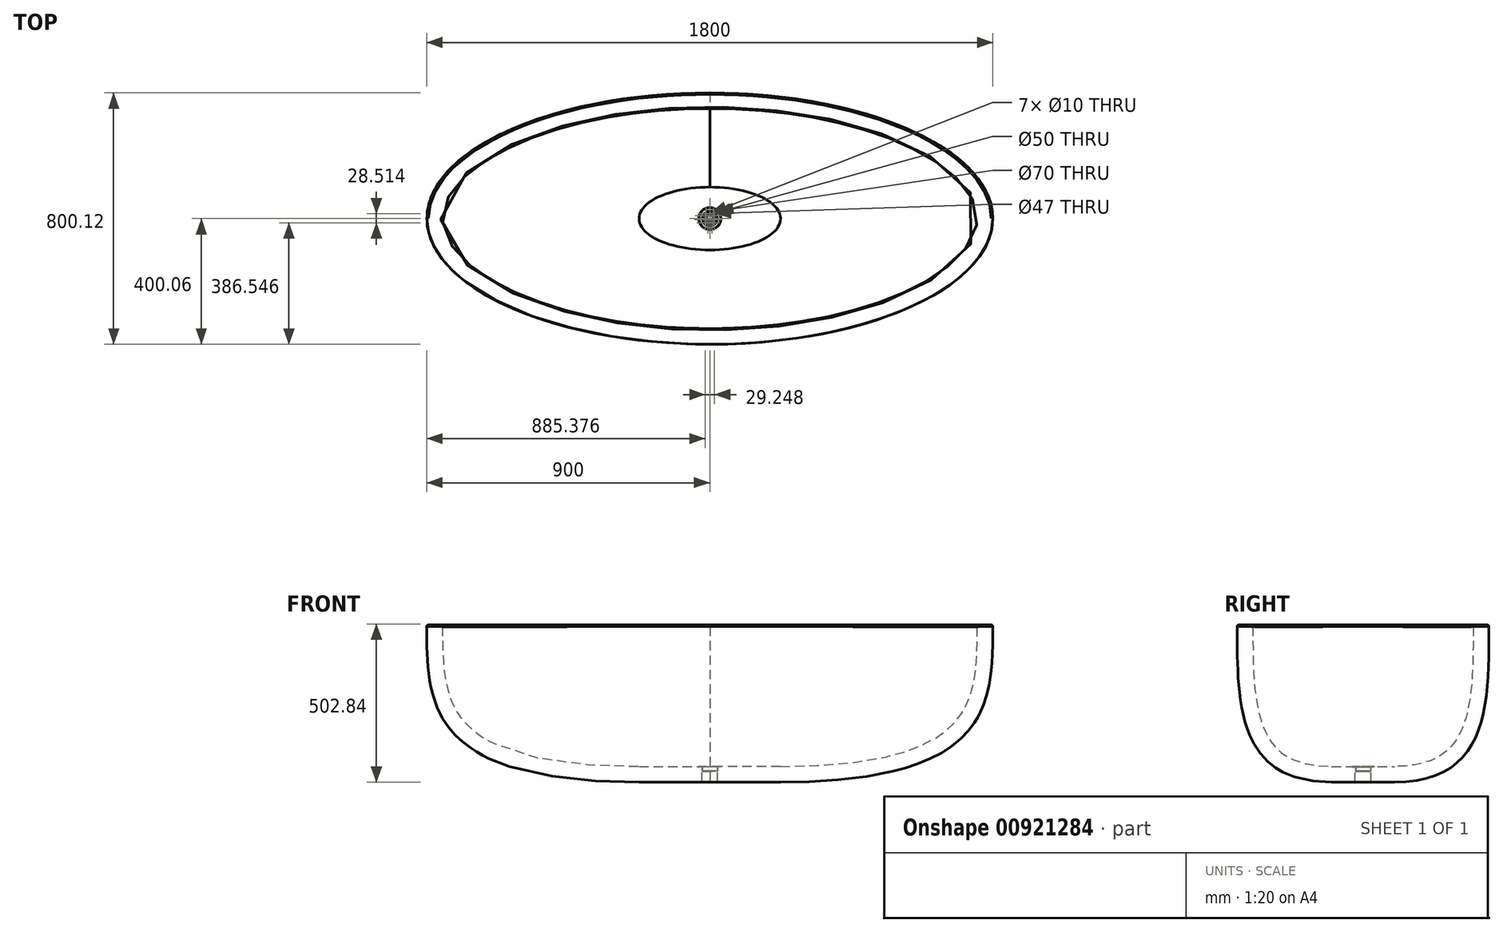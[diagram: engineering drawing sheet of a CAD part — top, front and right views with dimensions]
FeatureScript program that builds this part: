
annotation { "Feature Type Name" : "Feature", "Feature Type Description" : "" }
export const myFeature = defineFeature(function(context is Context, id is Id, definition is map)
    precondition{}
    {
        {
            var Q0;
            Q0=qCreatedBy(makeId("Top.planeOp"),FACE);
            cPlane(context, id + "F0", {"entities" : qUnion([Q0]), "cplaneType" : CPlaneType.OFFSET, "offset" : 500 * mm, "oppositeDirection" : true, "width" : 150 * mm, "height" : 150 * mm});
        }
        {
            var Q0;
            Q0=qCreatedBy(makeId("Top.planeOp"),FACE);
            var sketch = newSketch(context, id + "F1", { "sketchPlane" : qUnion([Q0])});
            skEllipse(sketch, "E0", {"center": v(0, 0) * mm, "majorRadius": 900 * mm, "minorRadius": 400 * mm, "majorAxis": v(-1, 0)});
            skSolve(sketch);
        }
        {
            var Q0;
            Q0=qCreatedBy(id+"F0.planeOp",FACE);
            var sketch = newSketch(context, id + "F2", { "sketchPlane" : qUnion([Q0])});
            skEllipse(sketch, "E1", {"center": v(0, 0) * mm, "majorRadius": 225 * mm, "minorRadius": 100 * mm, "majorAxis": v(1, 0)});
            skSolve(sketch);
        }
        {
            var Q0;
            Q0=qCreatedBy(makeId("Front.planeOp"),FACE);
            var sketch = newSketch(context, id + "F3", { "sketchPlane" : qUnion([Q0])});
            skLineSegment(sketch, "E2", {"start": v(0, 0) * mm, "end": v(-900, 0) * mm, "construction": true});
            skLineSegment(sketch, "E3", {"start": v(0, -500) * mm, "end": v(0, 0) * mm, "construction": true});
            skLineSegment(sketch, "E4", {"start": v(-225, -500) * mm, "end": v(-900, -500) * mm, "construction": true});
            skLineSegment(sketch, "E5", {"start": v(-900, 0) * mm, "end": v(-900, -500) * mm, "construction": true});
            skFitSpline(sketch, "E6", {"points": [v(-225, -500) * mm, v(-900, 0) * mm], "startDerivative": vector(-2025, 0) * mm, "endDerivative": vector(0, 750) * mm});
            skFitSpline(sketch, "E7.MirrorCS", {"points": [v(225, -500) * mm, v(900, 0) * mm], "startDerivative": vector(2025, 0) * mm, "endDerivative": vector(0, 750) * mm});
            skSolve(sketch);
        }
        {
            var Q0;
            Q0=qCreatedBy(makeId("Right.planeOp"),FACE);
            var sketch = newSketch(context, id + "F4", { "sketchPlane" : qUnion([Q0])});
            skLineSegment(sketch, "E8", {"start": v(0, 0) * mm, "end": v(-400, 0) * mm, "construction": true});
            skLineSegment(sketch, "E9", {"start": v(0, -376.84) * mm, "end": v(0, 0) * mm, "construction": true});
            skFitSpline(sketch, "E10.MirrorCS", {"points": [v(100, -500) * mm, v(400, 0) * mm], "startDerivative": vector(905.15, 0) * mm, "endDerivative": vector(-1.98, 750) * mm});
            skLineSegment(sketch, "E11", {"start": v(400, 0) * mm, "end": v(400, -665.48) * mm, "construction": true});
            skFitSpline(sketch, "E12.MirrorCS", {"points": [v(-100, -500) * mm, v(-400, 0) * mm], "startDerivative": vector(-905.15, 0) * mm, "endDerivative": vector(1.98, 750) * mm});
            skSolve(sketch);
        }
        {
            var Q0;
            Q0=makeQuery(id+"F1.imprint","IMPRINT",FACE,{"disambiguationData":[TD([[makeQuery(id+"F1.imprint","IMPRINT",EDGE,{"derivedFrom":sQuery(id+"F1.wireOp",EDGE,"E0")}),1.0]])]});
            var Q1;
            Q1=makeQuery(id+"F2.imprint","IMPRINT",FACE,{"disambiguationData":[TD([[makeQuery(id+"F2.imprint","IMPRINT",EDGE,{"derivedFrom":sQuery(id+"F2.wireOp",EDGE,"E1")}),1.0]])]});
            var Q2;
            Q2=sQuery(id+"F3.wireOp",EDGE,"E7.MirrorCS");
            var Q3;
            Q3=sQuery(id+"F4.wireOp",EDGE,"E10.MirrorCS");
            var Q4;
            Q4=sQuery(id+"F3.wireOp",EDGE,"E6");
            var Q5;
            Q5=sQuery(id+"F4.wireOp",EDGE,"E12.MirrorCS");
            loft(context, id + "F5", {"addGuides" : true, "sheetProfilesArray" : [{ "sheetProfileEntities" : qUnion([Q0]) }, { "sheetProfileEntities" : qUnion([Q1]) }], "guidesArray" : [{ "guideEntities" : qUnion([Q2]), "guideDerivativeType" : LoftGuideDerivativeType.DEFAULT, "guideDerivativeMagnitude" : 1 }, { "guideEntities" : qUnion([Q3]), "guideDerivativeType" : LoftGuideDerivativeType.DEFAULT, "guideDerivativeMagnitude" : 1 }, { "guideEntities" : qUnion([Q4]), "guideDerivativeType" : LoftGuideDerivativeType.DEFAULT, "guideDerivativeMagnitude" : 1 }, { "guideEntities" : qUnion([Q5]), "guideDerivativeType" : LoftGuideDerivativeType.DEFAULT, "guideDerivativeMagnitude" : 1 }]});
        }
        {
            var Q0;
            Q0=makeQuery(id+"F5.opLoft","CAP_FACE",FACE,{"disambiguationData":[OSD([makeQuery(id+"F1.imprint","IMPRINT",FACE,{"disambiguationData":[TD([[makeQuery(id+"F1.imprint","IMPRINT",EDGE,{"derivedFrom":sQuery(id+"F1.wireOp",EDGE,"E0")}),1.0]])]})])],"isStart":true});
            shell(context, id + "F6", {"entities" : qUnion([Q0]), "thickness" : 50 * mm});
        }
        {
            var Q0;
            Q0=makeQuery(id+"F6.opShell","OFFSET_EDGE",EDGE,{"disambiguationData":[OSD([sQuery(id+"F1.wireOp",EDGE,"E0"),sQuery(id+"F3.wireOp",EDGE,"9252d075-e4b6-4dbb-adb2-d72ff0bdb84f"),sQuery(id+"F3.wireOp",EDGE,"53aed624-99b1-4971-b216-df8eaaed4a5d0.MirrorCS"),sQuery(id+"F4.wireOp",EDGE,"d5f11650-ef26-4273-afc9-098c5ead0dd9"),sQuery(id+"F4.wireOp",EDGE,"256ece40-c806-4ca6-84fc-b8a8d223247b0.MirrorCS")])]});
            var Q1;
            Q1=makeQuery(id+"F5.opLoft","MID_CAP_EDGE",EDGE,{"disambiguationData":[OSD([sQuery(id+"F1.wireOp",EDGE,"E0"),sQuery(id+"F3.wireOp",EDGE,"53aed624-99b1-4971-b216-df8eaaed4a5d0.MirrorCS"),sQuery(id+"F4.wireOp",EDGE,"d5f11650-ef26-4273-afc9-098c5ead0dd9")])],"capPos":0.0});
            fillet(context, id + "F7", {"entities" : qUnion([Q0, Q1]), "radius" : 5 * mm, "tangentPropagation" : true, "allowEdgeOverflow" : false});
        }
        {
            var Q0;
            Q0=qCreatedBy(makeId("Top.planeOp"),FACE);
            var sketch = newSketch(context, id + "F8", { "sketchPlane" : qUnion([Q0])});
            skCircle(sketch, "E13", {"center": v(0, 0) * mm, "radius": 25 * mm});
            skSolve(sketch);
        }
        {
            var Q0;
            Q0 = qSketchRegion(id + "F8", true);
            extrude(context, id + "F9", {"entities" : qUnion([Q0]), "operationType" : NewBodyOperationType.REMOVE, "endBound" : BoundingType.THROUGH_ALL, "oppositeDirection" : true, "depth" : 25 * mm, "offsetDistance" : 25 * mm});
        }
        {
            var Q0;
            Q0=makeQuery(id+"F1.imprint","IMPRINT",FACE,{"disambiguationData":[TD([[makeQuery(id+"F1.imprint","IMPRINT",EDGE,{"derivedFrom":sQuery(id+"F1.wireOp",EDGE,"E0")}),1.0]])]});
            var sketch = newSketch(context, id + "F10", { "sketchPlane" : qUnion([Q0])});
            skCircle(sketch, "E14", {"center": v(0, 0) * mm, "radius": 35 * mm});
            skSolve(sketch);
        }
        {
            var Q0;
            Q0 = qSketchRegion(id + "F10", true);
            extrude(context, id + "F11", {"entities" : qUnion([Q0]), "operationType" : NewBodyOperationType.REMOVE, "oppositeDirection" : true, "depth" : 451.5 * mm, "offsetDistance" : 25 * mm});
        }
        {
            var Q0;
            Q0=makeQuery(id+"F11.boolean.opBoolean","INTERSECT",EDGE,{"derivedFrom":[makeQuery(id+"F6.opShell","OFFSET_FACE",FACE,{"disambiguationData":[OSD([makeQuery(id+"F2.imprint","IMPRINT",FACE,{"disambiguationData":[TD([[makeQuery(id+"F2.imprint","IMPRINT",EDGE,{"derivedFrom":sQuery(id+"F2.wireOp",EDGE,"E1")}),1.0]])]})])]}),makeQuery(id+"F11.opExtrude","SWEPT_FACE",FACE,{"disambiguationData":[OSD([sQuery(id+"F10.wireOp",EDGE,"E14")])]})]});
            var Q1;
            Q1=makeQuery(id+"F11.boolean.opBoolean","COPY",EDGE,{"derivedFrom":makeQuery(id+"F11.opExtrude","CAP_EDGE",EDGE,{"disambiguationData":[OSD([sQuery(id+"F10.wireOp",EDGE,"E14")])],"isStart":false})});
            var Q2;
            Q2=makeQuery(id+"F11.boolean.opBoolean","INTERSECT",EDGE,{"derivedFrom":[makeQuery(id+"F9.boolean.opBoolean","COPY",FACE,{"derivedFrom":makeQuery(id+"F9.opExtrude","SWEPT_FACE",FACE,{"disambiguationData":[OSD([sQuery(id+"F8.wireOp",EDGE,"E13")])]})}),makeQuery(id+"F11.opExtrude","CAP_FACE",FACE,{"disambiguationData":[OSD([sQuery(id+"F10.wireOp",EDGE,"E14")])],"isStart":false})]});
            fillet(context, id + "F12", {"entities" : qUnion([Q0, Q1, Q2]), "radius" : 0.5 * mm, "tangentPropagation" : true, "allowEdgeOverflow" : false});
        }
        {
            var Q0;
            Q0=qCreatedBy(makeId("Front.planeOp"),FACE);
            var sketch = newSketch(context, id + "F13", { "sketchPlane" : qUnion([Q0])});
            skLineSegment(sketch, "E15", {"start": v(-34.5, -450) * mm, "end": v(-34.5, -451) * mm});
            skLineSegment(sketch, "E16", {"start": v(-34.5, -451) * mm, "end": v(-25.5, -451) * mm});
            skLineSegment(sketch, "E17", {"start": v(-24.5, -452) * mm, "end": v(-24.5, -464.08) * mm});
            skLineSegment(sketch, "E18", {"start": v(-22.5, -466.08) * mm, "end": v(0, -466.08) * mm});
            skPoint(sketch, "E19.visualSharp", {"position": v(-24.5, -466.08) * mm});
            skArc(sketch, "E19.filletArc", {"start": v(-24.5, -464.08) * mm, "mid": v(-23.91, -465.5) * mm, "end": v(-22.5, -466.08) * mm});
            skPoint(sketch, "E20.visualSharp", {"position": v(-24.5, -451) * mm});
            skArc(sketch, "E20.filletArc", {"start": v(-24.5, -452) * mm, "mid": v(-24.8, -451.3) * mm, "end": v(-25.5, -451) * mm});
            skArc(sketch, "E21.0", {"start": v(-23.5, -452) * mm, "mid": v(-24.09, -450.59) * mm, "end": v(-25.5, -450) * mm});
            skLineSegment(sketch, "E21.1", {"start": v(-34.5, -450) * mm, "end": v(-25.5, -450) * mm});
            skLineSegment(sketch, "E22.0", {"start": v(-23.5, -452) * mm, "end": v(-23.5, -464.08) * mm});
            skPoint(sketch, "E23.visualSharp", {"position": v(-22.5, -466.08) * mm});
            skLineSegment(sketch, "E23.filletArc", {"start": v(-22.5, -466.08) * mm, "end": v(-22.5, -466.08) * mm});
            skLineSegment(sketch, "E24.0", {"start": v(-22.5, -465.08) * mm, "end": v(0, -465.08) * mm});
            skLineSegment(sketch, "E25", {"start": v(0, -465.08) * mm, "end": v(0, -466.08) * mm});
            skPoint(sketch, "E26.visualSharp", {"position": v(-23.5, -465.08) * mm});
            skArc(sketch, "E26.filletArc", {"start": v(-23.5, -464.08) * mm, "mid": v(-23.2, -464.79) * mm, "end": v(-22.5, -465.08) * mm});
            skLineSegment(sketch, "E27", {"start": v(0, -465.08) * mm, "end": v(0, -446.47) * mm, "construction": true});
            skSolve(sketch);
        }
        {
            var Q0;
            Q0 = qSketchRegion(id + "F13", true);
            var Q1;
            Q1=sQuery(id+"F13.wireOp",EDGE,"E27");
            var Q2;
            Q2=sQuery(id+"F13.wireOp",EDGE,"E17");
            var Q3;
            Q3=sQuery(id+"F13.wireOp",EDGE,"E19.filletArc");
            var Q4;
            Q4=sQuery(id+"F13.wireOp",EDGE,"E18");
            var Q5;
            Q5=sQuery(id+"F13.wireOp",EDGE,"E27");
            revolve(context, id + "F14", {"operationType" : NewBodyOperationType.ADD, "surfaceOperationType" : NewSurfaceOperationType.ADD, "entities" : qUnion([Q0]), "surfaceEntities" : qUnion([Q1, Q2, Q3, Q4]), "axis" : qUnion([Q5]), "revolveType" : RevolveType.FULL});
        }
        {
            var Q0;
            Q0=makeQuery(id+"F1.imprint","IMPRINT",FACE,{"disambiguationData":[TD([[makeQuery(id+"F1.imprint","IMPRINT",EDGE,{"derivedFrom":sQuery(id+"F1.wireOp",EDGE,"E0")}),1.0]])]});
            var sketch = newSketch(context, id + "F15", { "sketchPlane" : qUnion([Q0])});
            skCircle(sketch, "E28", {"center": v(0, 15) * mm, "radius": 5 * mm});
            skCircle(sketch, "E29.1.0", {"center": v(-11.73, 9.35) * mm, "radius": 5 * mm});
            skCircle(sketch, "E29.2.0", {"center": v(-14.62, -3.34) * mm, "radius": 5 * mm});
            skCircle(sketch, "E29.3.0", {"center": v(-6.5, -13.51) * mm, "radius": 5 * mm});
            skCircle(sketch, "E29.4.0", {"center": v(6.5, -13.51) * mm, "radius": 5 * mm});
            skCircle(sketch, "E29.5.0", {"center": v(14.62, -3.34) * mm, "radius": 5 * mm});
            skCircle(sketch, "E29.6.0", {"center": v(11.73, 9.35) * mm, "radius": 5 * mm});
            skPoint(sketch, "E29.center", {"position": v(0, 0) * mm});
            skSolve(sketch);
        }
        {
            var Q0;
            Q0 = qSketchRegion(id + "F15", true);
            extrude(context, id + "F16", {"entities" : qUnion([Q0]), "operationType" : NewBodyOperationType.REMOVE, "endBound" : BoundingType.THROUGH_ALL, "oppositeDirection" : true, "depth" : 25 * mm, "offsetDistance" : 25 * mm});
        }
    });
